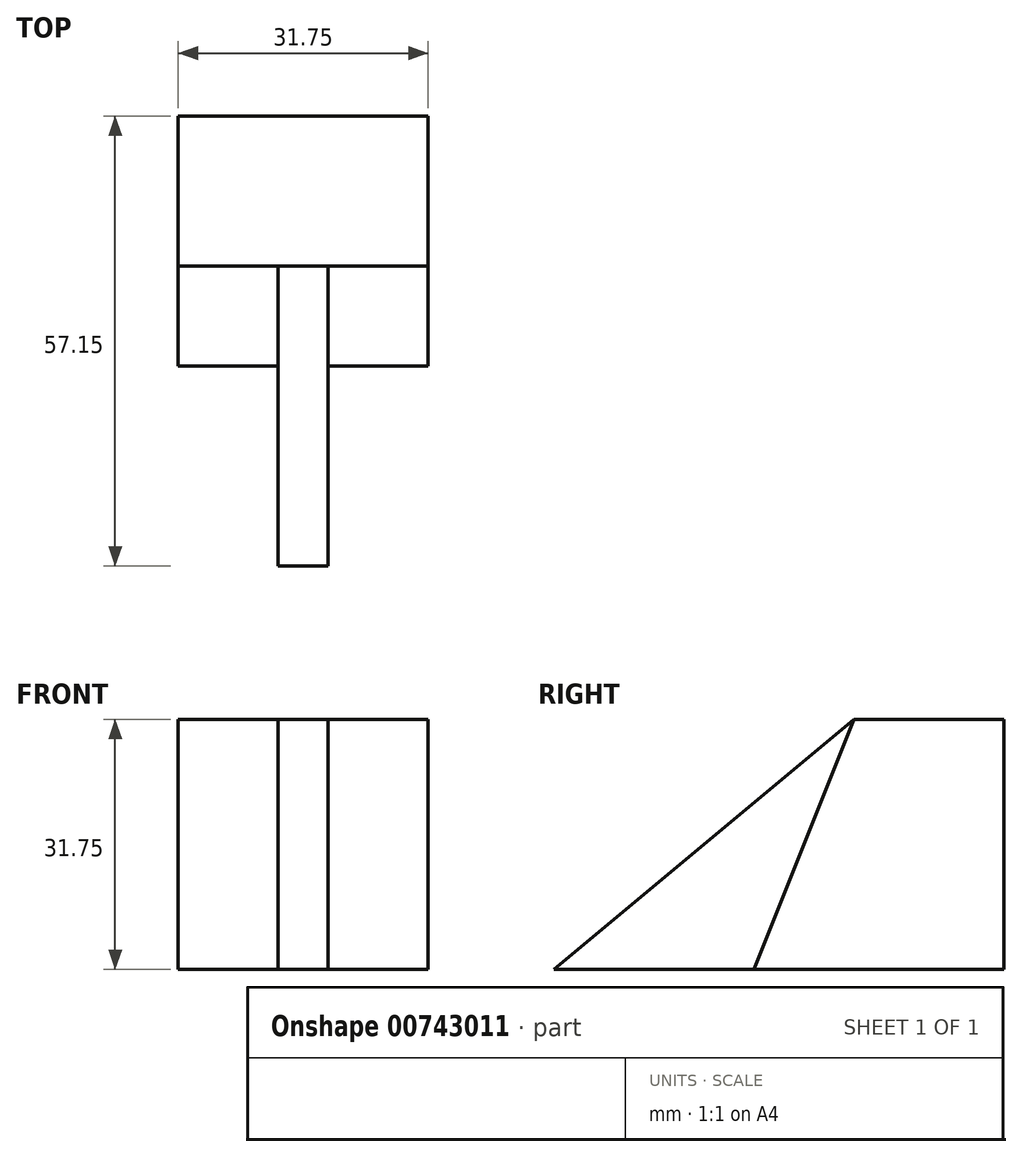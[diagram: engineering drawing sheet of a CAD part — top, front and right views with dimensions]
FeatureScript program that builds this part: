
annotation { "Feature Type Name" : "Feature", "Feature Type Description" : "" }
export const myFeature = defineFeature(function(context is Context, id is Id, definition is map)
    precondition{}
    {
        {
            var Q0;
            Q0=qCreatedBy(makeId("Front.planeOp"),FACE);
            var sketch = newSketch(context, id + "F0", { "sketchPlane" : qUnion([Q0])});
            skLineSegment(sketch, "E0", {"start": v(0, 0) * mm, "end": v(31.75, 0) * mm});
            skLineSegment(sketch, "E1", {"start": v(31.75, 0) * mm, "end": v(31.75, 31.75) * mm});
            skLineSegment(sketch, "E2", {"start": v(31.75, 31.75) * mm, "end": v(0, 31.75) * mm});
            skLineSegment(sketch, "E3", {"start": v(0, 31.75) * mm, "end": v(0, 0) * mm});
            skSolve(sketch);
        }
        {
            var Q0;
            Q0=makeQuery(id+"F0.imprint","IMPRINT",FACE,{"disambiguationData":[TD([[makeQuery(id+"F0.imprint","IMPRINT",EDGE,{"derivedFrom":sQuery(id+"F0.wireOp",EDGE,"E0")}),1.0]])]});
            extrude(context, id + "F1", {"entities" : qUnion([Q0]), "depth" : 57.15 * mm, "offsetDistance" : 25.4 * mm});
        }
        {
            var Q0;
            Q0=makeQuery(id+"F1.opExtrude","SWEPT_FACE",FACE,{"disambiguationData":[OSD([sQuery(id+"F0.wireOp",EDGE,"E3")])]});
            var sketch = newSketch(context, id + "F2", { "sketchPlane" : qUnion([Q0])});
            skLineSegment(sketch, "E4", {"start": v(19.05, 31.75) * mm, "end": v(31.75, 0) * mm});
            skLineSegment(sketch, "E5", {"start": v(31.75, 0) * mm, "end": v(57.15, 0) * mm});
            skLineSegment(sketch, "E6", {"start": v(57.15, 0) * mm, "end": v(57.15, 31.75) * mm});
            skLineSegment(sketch, "E7", {"start": v(57.15, 31.75) * mm, "end": v(19.05, 31.75) * mm});
            skSolve(sketch);
        }
        {
            var Q0;
            Q0=makeQuery(id+"F2.imprint","IMPRINT",FACE,{"disambiguationData":[TD([[makeQuery(id+"F2.imprint","IMPRINT",EDGE,{"derivedFrom":sQuery(id+"F2.wireOp",EDGE,"E4")}),1.0]])]});
            extrude(context, id + "F3", {"entities" : qUnion([Q0]), "operationType" : NewBodyOperationType.REMOVE, "oppositeDirection" : true, "depth" : 12.7 * mm, "offsetDistance" : 25.4 * mm});
        }
        {
            var Q0;
            Q0=makeQuery(id+"F1.opExtrude","SWEPT_FACE",FACE,{"disambiguationData":[OSD([sQuery(id+"F0.wireOp",EDGE,"E1")])]});
            var sketch = newSketch(context, id + "F4", { "sketchPlane" : qUnion([Q0])});
            skLineSegment(sketch, "E8", {"start": v(-19.05, 31.75) * mm, "end": v(-57.15, 0) * mm});
            skLineSegment(sketch, "E9", {"start": v(-57.15, 0) * mm, "end": v(-57.15, 31.75) * mm});
            skLineSegment(sketch, "E10", {"start": v(-57.15, 31.75) * mm, "end": v(-19.05, 31.75) * mm});
            skSolve(sketch);
        }
        {
            var Q0;
            Q0=makeQuery(id+"F4.imprint","IMPRINT",FACE,{"disambiguationData":[TD([[makeQuery(id+"F4.imprint","IMPRINT",EDGE,{"derivedFrom":sQuery(id+"F4.wireOp",EDGE,"E8")}),-1.0]])]});
            extrude(context, id + "F5", {"entities" : qUnion([Q0]), "operationType" : NewBodyOperationType.REMOVE, "oppositeDirection" : true, "depth" : 12.7 * mm, "offsetDistance" : 25.4 * mm});
        }
        {
            var Q0;
            Q0=makeQuery(id+"F5.boolean.opBoolean","COPY",FACE,{"derivedFrom":makeQuery(id+"F5.opExtrude","CAP_FACE",FACE,{"disambiguationData":[OSD([sQuery(id+"F4.wireOp",EDGE,"E8"),sQuery(id+"F4.wireOp",EDGE,"E9"),sQuery(id+"F4.wireOp",EDGE,"E10")])],"isStart":false})});
            var sketch = newSketch(context, id + "F6", { "sketchPlane" : qUnion([Q0])});
            skLineSegment(sketch, "E11", {"start": v(-57.15, 0) * mm, "end": v(-19.05, 31.75) * mm});
            skLineSegment(sketch, "E12", {"start": v(-19.05, 31.75) * mm, "end": v(-57.15, 31.75) * mm});
            skLineSegment(sketch, "E13", {"start": v(-57.15, 31.75) * mm, "end": v(-57.15, 0) * mm});
            skSolve(sketch);
        }
        {
            var Q0;
            Q0=makeQuery(id+"F6.imprint","IMPRINT",FACE,{"disambiguationData":[TD([[makeQuery(id+"F6.imprint","IMPRINT",EDGE,{"derivedFrom":sQuery(id+"F6.wireOp",EDGE,"E11")}),-1.0]])]});
            extrude(context, id + "F7", {"entities" : qUnion([Q0]), "operationType" : NewBodyOperationType.REMOVE, "oppositeDirection" : true, "depth" : 12.7 * mm, "offsetDistance" : 25.4 * mm});
        }
        {
            var Q0;
            Q0=makeQuery(id+"F1.opExtrude","SWEPT_FACE",FACE,{"disambiguationData":[OSD([sQuery(id+"F0.wireOp",EDGE,"E1")])]});
            var sketch = newSketch(context, id + "F8", { "sketchPlane" : qUnion([Q0])});
            skLineSegment(sketch, "E14", {"start": v(-19.05, 31.75) * mm, "end": v(-31.75, 0) * mm});
            skLineSegment(sketch, "E15", {"start": v(-31.75, 0) * mm, "end": v(-57.15, 0) * mm});
            skLineSegment(sketch, "E16", {"start": v(-57.15, 0) * mm, "end": v(-19.05, 31.75) * mm});
            skSolve(sketch);
        }
        {
            var Q0;
            Q0=makeQuery(id+"F8.imprint","IMPRINT",FACE,{"disambiguationData":[TD([[makeQuery(id+"F8.imprint","IMPRINT",EDGE,{"derivedFrom":sQuery(id+"F8.wireOp",EDGE,"E14")}),-1.0]])]});
            extrude(context, id + "F9", {"entities" : qUnion([Q0]), "operationType" : NewBodyOperationType.REMOVE, "oppositeDirection" : true, "depth" : 12.7 * mm, "offsetDistance" : 25.4 * mm});
        }
    });
